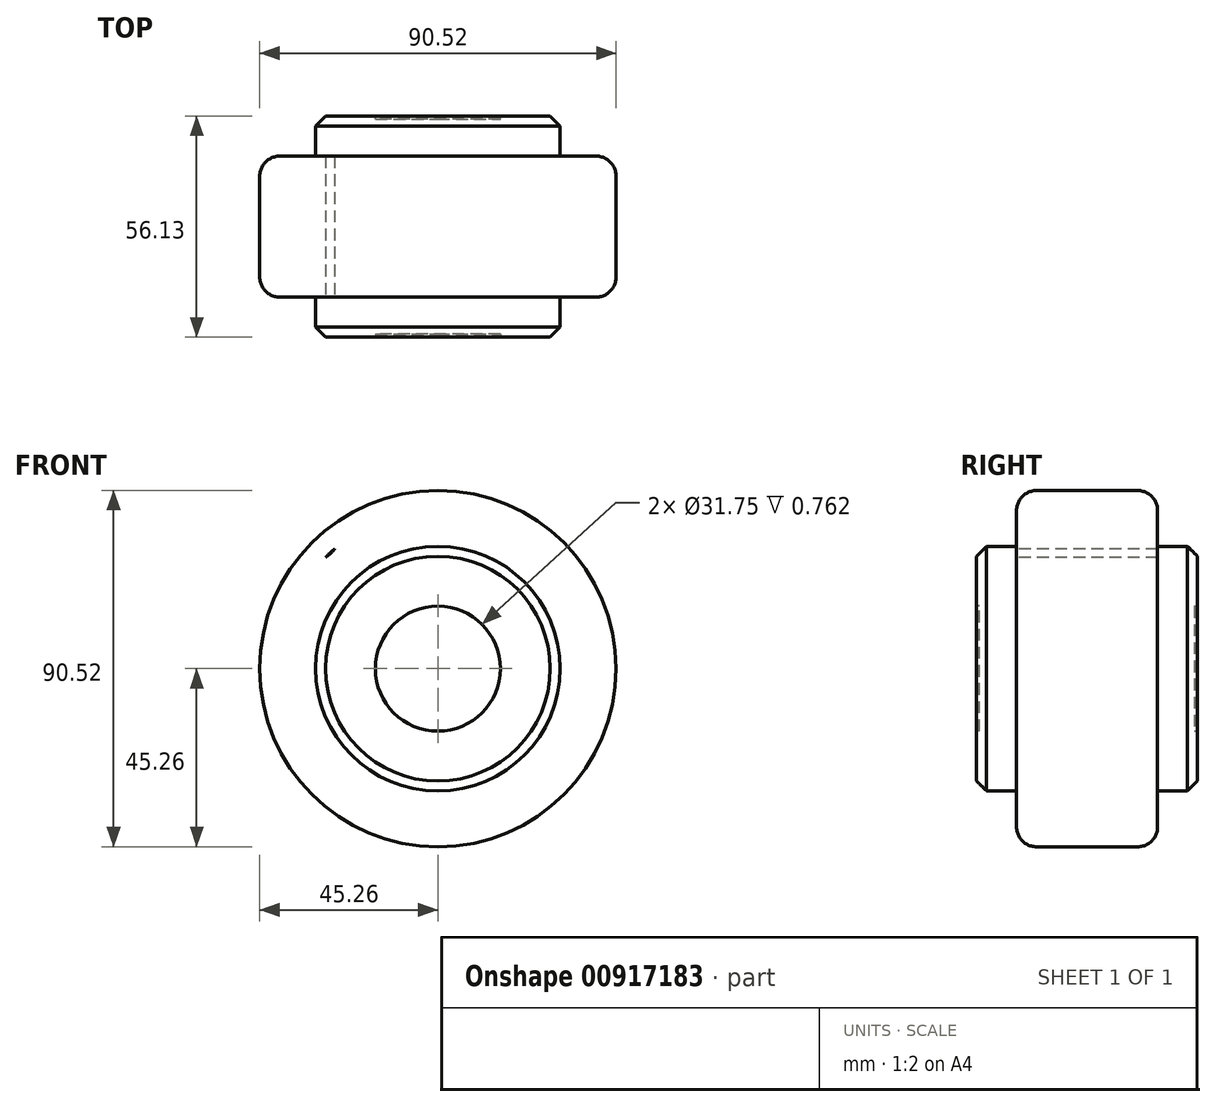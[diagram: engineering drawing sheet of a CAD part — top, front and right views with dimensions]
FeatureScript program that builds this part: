
annotation { "Feature Type Name" : "Feature", "Feature Type Description" : "" }
export const myFeature = defineFeature(function(context is Context, id is Id, definition is map)
    precondition{}
    {
        {
            var Q0;
            Q0=qCreatedBy(makeId("Front.planeOp"),FACE);
            var sketch = newSketch(context, id + "F0", { "sketchPlane" : qUnion([Q0])});
            skCircle(sketch, "E0", {"center": v(0, 0) * mm, "radius": 45.26 * mm});
            skSolve(sketch);
        }
        {
            var Q0;
            Q0 = qSketchRegion(id + "F0", true);
            extrude(context, id + "F1", {"entities" : qUnion([Q0]), "depth" : 35.81 * mm, "offsetDistance" : 25.4 * mm});
        }
        {
            var Q0;
            Q0=makeQuery(id+"F1.opExtrude","CAP_FACE",FACE,{"disambiguationData":[OSD([sQuery(id+"F0.wireOp",EDGE,"E0")])],"isStart":false});
            var Q1;
            Q1=makeQuery(id+"F1.opExtrude","CAP_EDGE",EDGE,{"disambiguationData":[OSD([sQuery(id+"F0.wireOp",EDGE,"E0")])],"isStart":true});
            fillet(context, id + "F2", {"entities" : qUnion([Q0, Q1]), "radius" : 5.08 * mm, "tangentPropagation" : true, "allowEdgeOverflow" : false});
        }
        {
            var Q0;
            Q0=makeQuery(id+"F1.opExtrude","CAP_FACE",FACE,{"disambiguationData":[OSD([sQuery(id+"F0.wireOp",EDGE,"E0")])],"isStart":false});
            var sketch = newSketch(context, id + "F3", { "sketchPlane" : qUnion([Q0])});
            skCircle(sketch, "E1", {"center": v(0, 0) * mm, "radius": 31.08 * mm});
            skSolve(sketch);
        }
        {
            var Q0;
            Q0 = qSketchRegion(id + "F3", true);
            extrude(context, id + "F4", {"entities" : qUnion([Q0]), "operationType" : NewBodyOperationType.ADD, "depth" : 10.16 * mm, "offsetDistance" : 25.4 * mm});
        }
        {
            var Q0;
            Q0=makeQuery(id+"F4.opExtrude","CAP_EDGE",EDGE,{"disambiguationData":[OSD([sQuery(id+"F3.wireOp",EDGE,"E1")])],"isStart":false});
            chamfer(context, id + "F5", {"entities" : qUnion([Q0]), "width" : 2.54 * mm, "tangentPropagation" : true});
        }
        {
            var Q0;
            Q0=makeQuery(id+"F1.opExtrude","CAP_FACE",FACE,{"disambiguationData":[OSD([sQuery(id+"F0.wireOp",EDGE,"E0")])],"isStart":true});
            var sketch = newSketch(context, id + "F6", { "sketchPlane" : qUnion([Q0])});
            skSolve(sketch);
        }
        {
            var Q0;
            {var subQ0=sQuery(id+"F0.wireOp",EDGE,"E0");Q0=makeQuery(id+"F6.imprint","IMPRINT",FACE,{"disambiguationData":[TD([[makeQuery(id+"F6.imprint","IMPRINT",EDGE,{"derivedFrom":makeQuery(id+"F2.opFillet","BLEND_EDGE",EDGE,{"blendedFrom":[makeQuery(id+"F1.opExtrude","CAP_EDGE",EDGE,{"disambiguationData":[OSD([subQ0])],"isStart":true}),makeQuery(id+"F1.opExtrude","CAP_FACE",FACE,{"disambiguationData":[OSD([subQ0])],"isStart":true})],"blendedInto":[makeQuery(id+"F1.opExtrude","CAP_FACE",FACE,{"disambiguationData":[OSD([subQ0])],"isStart":true})]})}),1.0]])]});}
            var sketch = newSketch(context, id + "F7", { "sketchPlane" : qUnion([Q0])});
            skCircle(sketch, "E2", {"center": v(0, 0) * mm, "radius": 31.08 * mm});
            skSolve(sketch);
        }
        {
            var Q0;
            Q0=makeQuery(id+"F7.imprint","IMPRINT",FACE,{"disambiguationData":[TD([[makeQuery(id+"F7.imprint","IMPRINT",EDGE,{"derivedFrom":sQuery(id+"F7.wireOp",EDGE,"E2")}),1.0]])]});
            extrude(context, id + "F8", {"entities" : qUnion([Q0]), "operationType" : NewBodyOperationType.ADD, "depth" : 10.16 * mm, "offsetDistance" : 25.4 * mm});
        }
        {
            var Q0;
            Q0=makeQuery(id+"F8.opExtrude","CAP_EDGE",EDGE,{"disambiguationData":[OSD([sQuery(id+"F7.wireOp",EDGE,"E2")])],"isStart":false});
            chamfer(context, id + "F9", {"entities" : qUnion([Q0]), "width" : 2.54 * mm, "tangentPropagation" : true});
        }
        {
            var Q0;
            Q0=makeQuery(id+"F8.opExtrude","CAP_FACE",FACE,{"disambiguationData":[OSD([sQuery(id+"F7.wireOp",EDGE,"E2")])],"isStart":false});
            var sketch = newSketch(context, id + "F10", { "sketchPlane" : qUnion([Q0])});
            skCircle(sketch, "E3", {"center": v(0, 0) * mm, "radius": 15.88 * mm});
            skSolve(sketch);
        }
        {
            var Q0;
            Q0=makeQuery(id+"F10.imprint","IMPRINT",FACE,{"disambiguationData":[TD([[makeQuery(id+"F10.imprint","IMPRINT",EDGE,{"derivedFrom":sQuery(id+"F10.wireOp",EDGE,"E3")}),1.0]])]});
            extrude(context, id + "F11", {"entities" : qUnion([Q0]), "operationType" : NewBodyOperationType.REMOVE, "oppositeDirection" : true, "depth" : 0.76 * mm, "offsetDistance" : 25.4 * mm});
        }
        {
            var Q0;
            Q0=makeQuery(id+"F4.opExtrude","CAP_FACE",FACE,{"disambiguationData":[OSD([sQuery(id+"F3.wireOp",EDGE,"E1")])],"isStart":false});
            var sketch = newSketch(context, id + "F12", { "sketchPlane" : qUnion([Q0])});
            skCircle(sketch, "E4", {"center": v(0, 0) * mm, "radius": 15.88 * mm});
            skSolve(sketch);
        }
        {
            var Q0;
            Q0=makeQuery(id+"F12.imprint","IMPRINT",FACE,{"disambiguationData":[TD([[makeQuery(id+"F12.imprint","IMPRINT",EDGE,{"derivedFrom":sQuery(id+"F12.wireOp",EDGE,"E4")}),1.0]])]});
            extrude(context, id + "F13", {"entities" : qUnion([Q0]), "operationType" : NewBodyOperationType.REMOVE, "oppositeDirection" : true, "depth" : 0.76 * mm, "offsetDistance" : 25.4 * mm});
        }
        {
            var Q0;
            Q0=makeQuery(id+"F1.opExtrude","CAP_FACE",FACE,{"disambiguationData":[OSD([sQuery(id+"F0.wireOp",EDGE,"E0")])],"isStart":false});
            var sketch = newSketch(context, id + "F14", { "sketchPlane" : qUnion([Q0])});
            skFitSpline(sketch, "E5", {"points": [v(-7.47, 39.48) * mm, v(-21.37, 41.24) * mm, v(-26.22, 30.44) * mm, v(-40.07, 20.91) * mm, v(-40.02, 3.64) * mm, v(-43.07, -15.38) * mm, v(-32.77, -23.26) * mm, v(-25.21, -39.03) * mm, v(-12.64, -38.14) * mm, v(0, -46.98) * mm, v(10.3, -38.84) * mm, v(24.82, -40.2) * mm, v(29.3, -27.5) * mm, v(40.07, -23.4) * mm, v(39.2, -8.85) * mm, v(47.24, 5.8) * mm, v(36.9, 15.9) * mm, v(36.42, 30.69) * mm, v(20.82, 34.37) * mm, v(8.4, 46.06) * mm, v(-7.47, 39.48) * mm]});
            skCircle(sketch, "E6", {"center": v(0, 0) * mm, "radius": 40.18 * mm});
            skCircle(sketch, "E7", {"center": v(0, 0) * mm, "radius": 47.63 * mm});
            skSolve(sketch);
        }
        {
            var Q0;
            {var subQ0=sQuery(id+"F14.wireOp",EDGE,"E6");var subQ1=sQuery(id+"F14.wireOp",EDGE,"E5");var subQ12=makeQuery(id+"F14.imprint","INTERSECT",VERTEX,{"disambiguationData":[OD(6.0)],"derivedFrom":[subQ1,subQ0]});Q0=makeQuery(id+"F14.imprint","IMPRINT",FACE,{"disambiguationData":[TD([[makeQuery(id+"F14.imprint","IMPRINT",EDGE,{"disambiguationData":[TD([[subQ12,1.0]])],"derivedFrom":subQ1}),-1.0]])]});}
            extrude(context, id + "F15", {"entities" : qUnion([Q0]), "operationType" : NewBodyOperationType.REMOVE, "oppositeDirection" : true, "depth" : 61.72 * mm, "offsetDistance" : 25.4 * mm});
        }
    });
